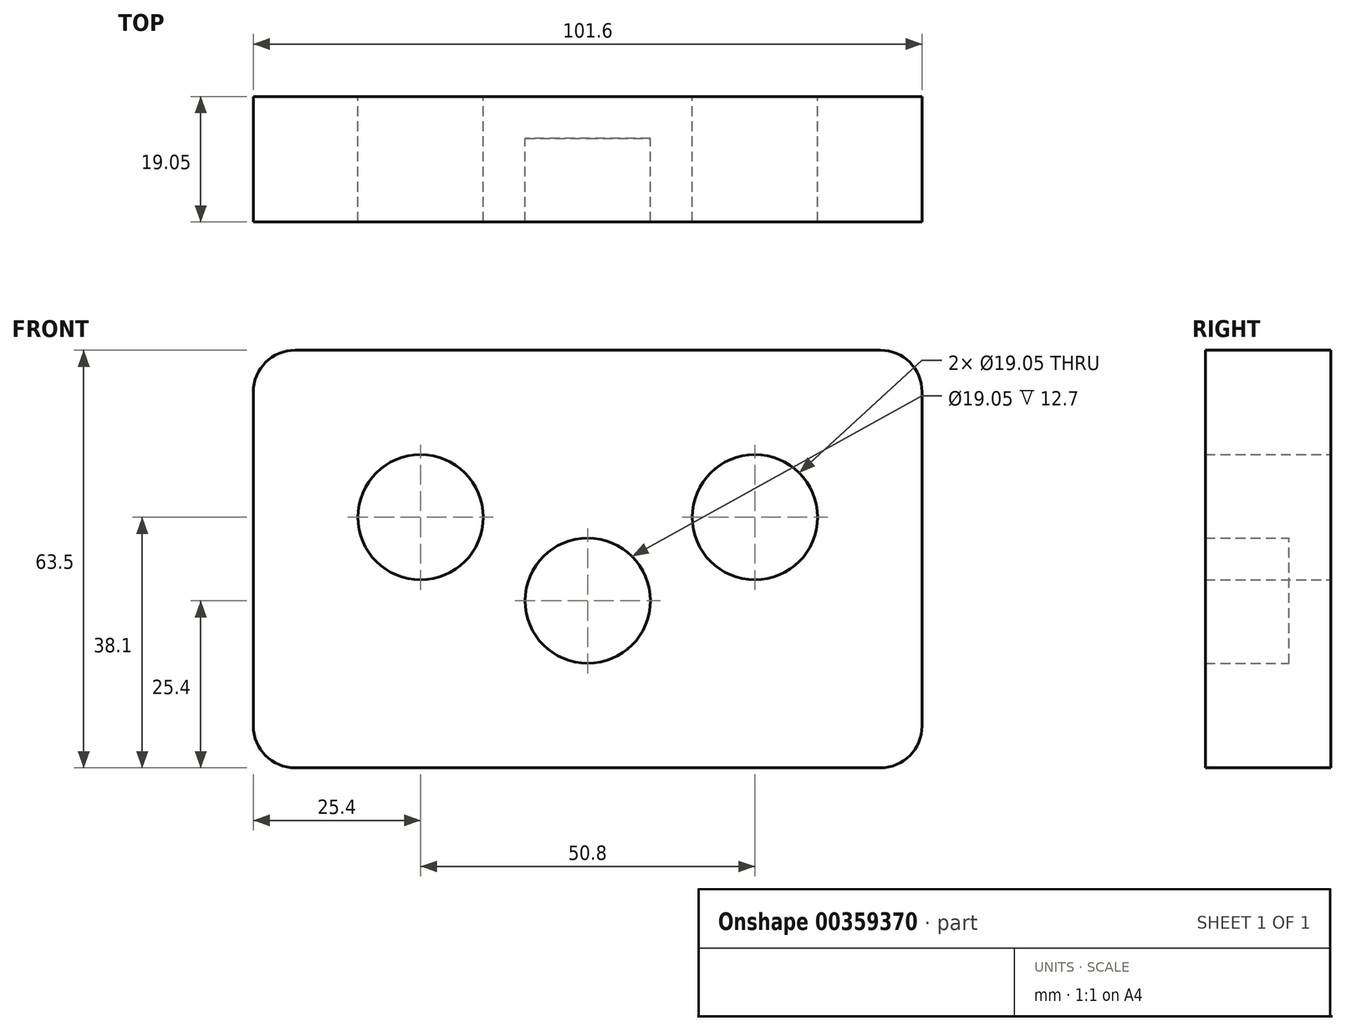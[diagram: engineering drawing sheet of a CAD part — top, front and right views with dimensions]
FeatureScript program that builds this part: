
annotation { "Feature Type Name" : "Feature", "Feature Type Description" : "" }
export const myFeature = defineFeature(function(context is Context, id is Id, definition is map)
    precondition{}
    {
        {
            var Q0;
            Q0=qCreatedBy(makeId("Front.planeOp"),FACE);
            var sketch = newSketch(context, id + "F0", { "sketchPlane" : qUnion([Q0])});
            skLineSegment(sketch, "E0.bottom", {"start": v(-50.8, 31.75) * mm, "end": v(50.8, 31.75) * mm});
            skLineSegment(sketch, "E0.top", {"start": v(-50.8, -31.75) * mm, "end": v(50.8, -31.75) * mm});
            skLineSegment(sketch, "E0.left", {"start": v(-50.8, 31.75) * mm, "end": v(-50.8, -31.75) * mm});
            skLineSegment(sketch, "E0.right", {"start": v(50.8, 31.75) * mm, "end": v(50.8, -31.75) * mm});
            skPoint(sketch, "E0.middle", {"position": v(0, 0) * mm});
            skLineSegment(sketch, "E1", {"start": v(50.8, 31.75) * mm, "end": v(50.8, 6.35) * mm});
            skLineSegment(sketch, "E2", {"start": v(50.8, 6.35) * mm, "end": v(25.4, 6.35) * mm});
            skLineSegment(sketch, "E3", {"start": v(-50.8, 31.75) * mm, "end": v(-50.8, 6.35) * mm});
            skLineSegment(sketch, "E4", {"start": v(-50.8, 6.35) * mm, "end": v(-25.4, 6.35) * mm});
            skLineSegment(sketch, "E5", {"start": v(-50.8, -31.75) * mm, "end": v(0, -31.75) * mm});
            skLineSegment(sketch, "E6", {"start": v(0, -31.75) * mm, "end": v(0, -6.35) * mm});
            skCircle(sketch, "E7", {"center": v(-25.4, 6.35) * mm, "radius": 9.53 * mm});
            skCircle(sketch, "E8", {"center": v(0, -6.35) * mm, "radius": 9.53 * mm});
            skCircle(sketch, "E9", {"center": v(25.4, 6.35) * mm, "radius": 9.53 * mm});
            skLineSegment(sketch, "E10", {"start": v(0, -31.75) * mm, "end": v(-9.53, -31.75) * mm});
            skLineSegment(sketch, "E11", {"start": v(0, -31.75) * mm, "end": v(9.53, -31.75) * mm});
            skLineSegment(sketch, "E12", {"start": v(-9.53, -31.75) * mm, "end": v(-9.53, -120.05) * mm});
            skLineSegment(sketch, "E13", {"start": v(9.53, -31.75) * mm, "end": v(9.53, -119.66) * mm});
            skLineSegment(sketch, "E14", {"start": v(9.53, -119.66) * mm, "end": v(-9.53, -120.05) * mm});
            skSolve(sketch);
        }
        {
            var Q0;
            Q0=makeQuery(id+"F0.imprint","IMPRINT",FACE,{"disambiguationData":[TD([[makeQuery(id+"F0.imprint","IMPRINT",EDGE,{"derivedFrom":sQuery(id+"F0.wireOp",EDGE,"E0.bottom")}),-1.0]])]});
            var Q1;
            Q1=makeQuery(id+"F0.imprint","IMPRINT",FACE,{"disambiguationData":[TD([[makeQuery(id+"F0.imprint","IMPRINT",EDGE,{"derivedFrom":sQuery(id+"F0.wireOp",EDGE,"E10")}),1.0]])]});
            var Q2;
            Q2=makeQuery(id+"F0.imprint","IMPRINT",FACE,{"disambiguationData":[TD([[makeQuery(id+"F0.imprint","IMPRINT",EDGE,{"derivedFrom":sQuery(id+"F0.wireOp",EDGE,"E8")}),1.0]])]});
            extrude(context, id + "F1", {"entities" : qUnion([Q0, Q1, Q2]), "depth" : 87.96 * mm});
        }
        {
            var Q0;
            Q0=makeQuery(id+"F1.opExtrude","SWEPT_FACE",FACE,{"disambiguationData":[OSD([sQuery(id+"F0.wireOp",EDGE,"E0.right"),sQuery(id+"F0.wireOp",EDGE,"E1")])]});
            var sketch = newSketch(context, id + "F2", { "sketchPlane" : qUnion([Q0])});
            skLineSegment(sketch, "E15.bottom", {"start": v(0, 31.75) * mm, "end": v(-19.05, 31.75) * mm});
            skLineSegment(sketch, "E15.top", {"start": v(0, -31.75) * mm, "end": v(-19.05, -31.75) * mm});
            skLineSegment(sketch, "E15.left", {"start": v(0, 31.75) * mm, "end": v(0, -31.75) * mm});
            skLineSegment(sketch, "E15.right", {"start": v(-19.05, 31.75) * mm, "end": v(-19.05, -31.75) * mm});
            skLineSegment(sketch, "E16", {"start": v(-19.05, -31.75) * mm, "end": v(-11.43, -31.75) * mm});
            skLineSegment(sketch, "E17.top", {"start": v(-19.05, -50.3) * mm, "end": v(-11.43, -50.3) * mm});
            skLineSegment(sketch, "E17.left", {"start": v(-19.05, -31.75) * mm, "end": v(-19.05, -50.3) * mm});
            skLineSegment(sketch, "E17.right", {"start": v(-11.43, -31.75) * mm, "end": v(-11.43, -50.3) * mm});
            skLineSegment(sketch, "E18", {"start": v(-87.96, 31.75) * mm, "end": v(-87.96, -31.75) * mm});
            skLineSegment(sketch, "E19", {"start": v(-87.96, -31.75) * mm, "end": v(-87.96, -63.83) * mm});
            skArc(sketch, "E20", {"start": v(-87.96, -63.83) * mm, "mid": v(-43.94, -89.6) * mm, "end": v(-11.43, -50.3) * mm});
            skLineSegment(sketch, "E21", {"start": v(-87.96, -63.83) * mm, "end": v(-80.34, -63.83) * mm});
            skArc(sketch, "E22", {"start": v(-80.34, -63.83) * mm, "mid": v(-44.26, -81.68) * mm, "end": v(-19.05, -50.3) * mm});
            skLineSegment(sketch, "E23.bottom", {"start": v(-118.34, 65.4) * mm, "end": v(41.55, 65.4) * mm});
            skLineSegment(sketch, "E23.top", {"start": v(-118.34, -123.07) * mm, "end": v(41.55, -123.07) * mm});
            skLineSegment(sketch, "E23.left", {"start": v(-118.34, 65.4) * mm, "end": v(-118.34, -123.07) * mm});
            skLineSegment(sketch, "E23.right", {"start": v(41.55, 65.4) * mm, "end": v(41.55, -123.07) * mm});
            skSolve(sketch);
        }
        {
            var Q0;
            {var subQ1=sQuery(id+"F2.wireOp",EDGE,"E15.bottom");Q0=makeQuery(id+"F2.imprint","IMPRINT",FACE,{"disambiguationData":[TD([[makeQuery(id+"F2.imprint","IMPRINT",EDGE,{"derivedFrom":subQ1}),1.0]])]});}
            var Q1;
            {var subQ0=sQuery(id+"F2.wireOp",EDGE,"E15.right");Q1=makeQuery(id+"F2.imprint","IMPRINT",FACE,{"disambiguationData":[TD([[makeQuery(id+"F2.imprint","IMPRINT",EDGE,{"derivedFrom":subQ0}),-1.0]])]});}
            var Q2;
            {var subQ1=sQuery(id+"F2.wireOp",EDGE,"E17.left");Q2=makeQuery(id+"F2.imprint","IMPRINT",FACE,{"disambiguationData":[TD([[makeQuery(id+"F2.imprint","IMPRINT",EDGE,{"derivedFrom":subQ1}),-1.0]])]});}
            extrude(context, id + "F3", {"entities" : qUnion([Q0, Q1, Q2]), "operationType" : NewBodyOperationType.REMOVE, "endBound" : BoundingType.THROUGH_ALL, "oppositeDirection" : true, "depth" : 25.4 * mm});
        }
        {
            var Q0;
            Q0=makeQuery(id+"F1.opExtrude","SWEPT_EDGE",EDGE,{"disambiguationData":[OSD([sQuery(id+"F0.wireOp",EDGE,"E0.bottom"),sQuery(id+"F0.wireOp",EDGE,"E3")])]});
            var Q1;
            Q1=makeQuery(id+"F1.opExtrude","SWEPT_EDGE",EDGE,{"disambiguationData":[OSD([sQuery(id+"F0.wireOp",EDGE,"E0.bottom"),sQuery(id+"F0.wireOp",EDGE,"E1")])]});
            var Q2;
            Q2=makeQuery(id+"F1.opExtrude","SWEPT_EDGE",EDGE,{"disambiguationData":[OSD([sQuery(id+"F0.wireOp",EDGE,"E0.top"),sQuery(id+"F0.wireOp",EDGE,"E0.right")])]});
            var Q3;
            Q3=makeQuery(id+"F1.opExtrude","SWEPT_EDGE",EDGE,{"disambiguationData":[OSD([sQuery(id+"F0.wireOp",EDGE,"E0.left"),sQuery(id+"F0.wireOp",EDGE,"E5")])]});
            var Q4;
            Q4=makeQuery(id+"F3.boolean.opBoolean","INTERSECT",EDGE,{"derivedFrom":[makeQuery(id+"F1.opExtrude","SWEPT_FACE",FACE,{"disambiguationData":[OSD([sQuery(id+"F0.wireOp",EDGE,"E12")])]}),makeQuery(id+"F3.opExtrude","SWEPT_FACE",FACE,{"disambiguationData":[OSD([sQuery(id+"F2.wireOp",EDGE,"E21")])]})]});
            var Q5;
            Q5=makeQuery(id+"F3.boolean.opBoolean","INTERSECT",EDGE,{"derivedFrom":[makeQuery(id+"F1.opExtrude","SWEPT_FACE",FACE,{"disambiguationData":[OSD([sQuery(id+"F0.wireOp",EDGE,"E13")])]}),makeQuery(id+"F3.opExtrude","SWEPT_FACE",FACE,{"disambiguationData":[OSD([sQuery(id+"F2.wireOp",EDGE,"E21")])]})]});
            fillet(context, id + "F4", {"entities" : qUnion([Q0, Q1, Q2, Q3, Q4, Q5]), "radius" : 6.35 * mm, "tangentPropagation" : true, "allowEdgeOverflow" : false});
        }
        {
            var Q0;
            Q0=makeQuery(id+"F0.imprint","IMPRINT",FACE,{"disambiguationData":[TD([[makeQuery(id+"F0.imprint","IMPRINT",EDGE,{"derivedFrom":sQuery(id+"F0.wireOp",EDGE,"E8")}),1.0]])]});
            extrude(context, id + "F5", {"entities" : qUnion([Q0]), "operationType" : NewBodyOperationType.REMOVE, "endBound" : BoundingType.THROUGH_ALL, "depth" : 25.4 * mm});
        }
        {
            var Q0;
            Q0=makeQuery(id+"F0.imprint","IMPRINT",FACE,{"disambiguationData":[TD([[makeQuery(id+"F0.imprint","IMPRINT",EDGE,{"derivedFrom":sQuery(id+"F0.wireOp",EDGE,"E8")}),1.0]])]});
            extrude(context, id + "F6", {"entities" : qUnion([Q0]), "operationType" : NewBodyOperationType.ADD, "depth" : 6.35 * mm});
        }
    });
